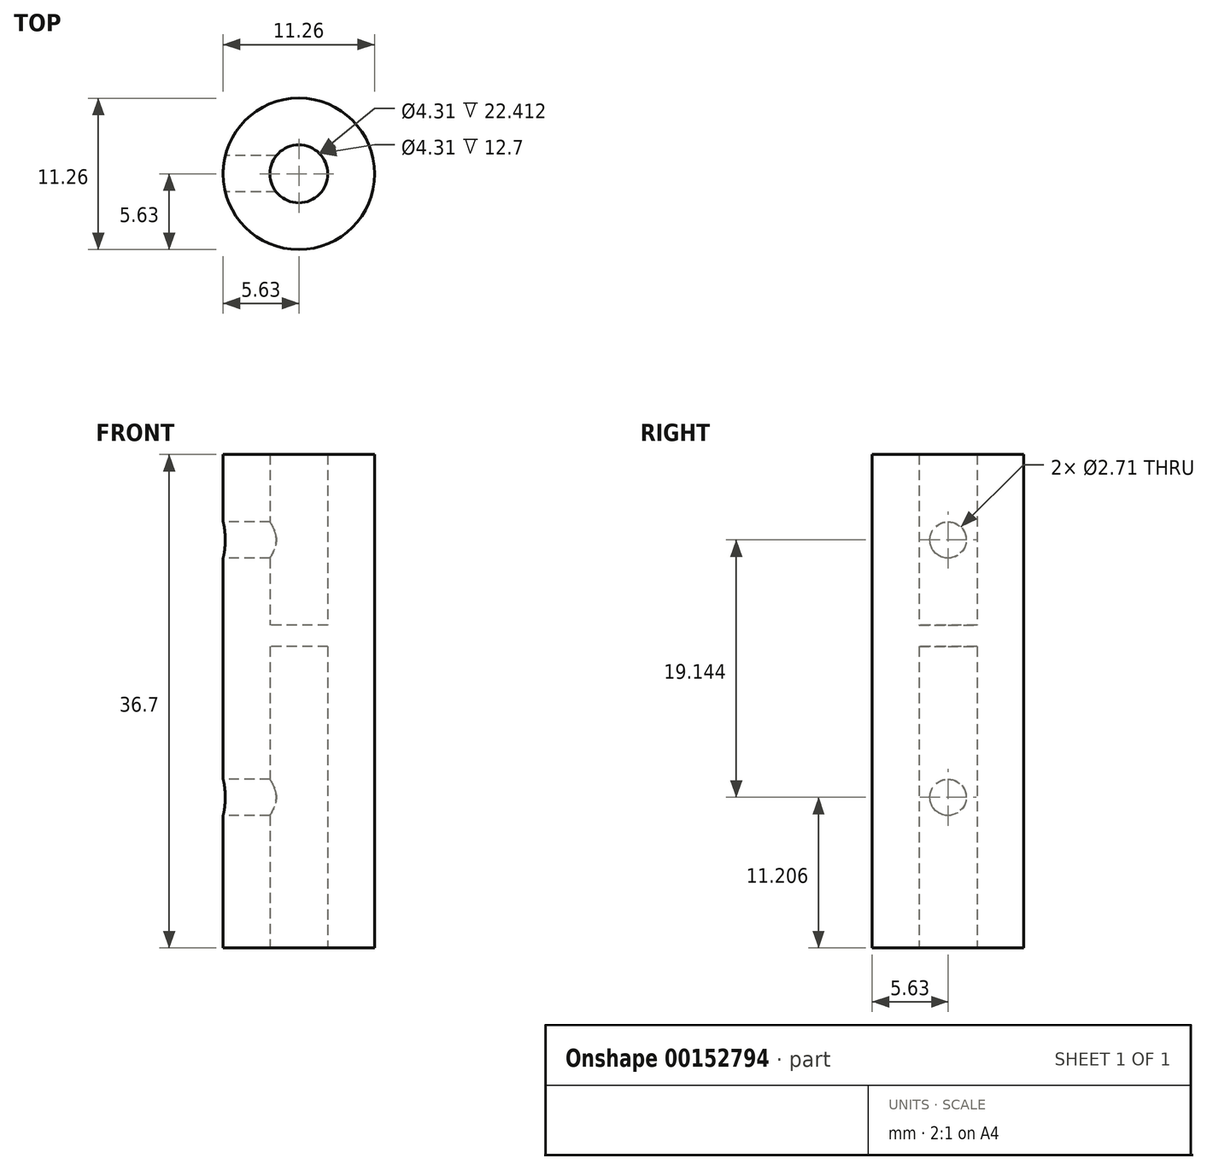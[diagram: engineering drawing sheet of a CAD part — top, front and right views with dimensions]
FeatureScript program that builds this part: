
annotation { "Feature Type Name" : "Feature", "Feature Type Description" : "" }
export const myFeature = defineFeature(function(context is Context, id is Id, definition is map)
    precondition{}
    {
        {
            var Q0;
            Q0=qCreatedBy(makeId("Top.planeOp"),FACE);
            var sketch = newSketch(context, id + "F0", { "sketchPlane" : qUnion([Q0])});
            skLineSegment(sketch, "E0.bottom", {"start": v(5.63, -5.63) * mm, "end": v(-5.63, -5.63) * mm});
            skLineSegment(sketch, "E0.top", {"start": v(5.63, 5.63) * mm, "end": v(-5.63, 5.63) * mm});
            skLineSegment(sketch, "E0.left", {"start": v(5.63, -5.63) * mm, "end": v(5.63, 5.63) * mm});
            skLineSegment(sketch, "E0.right", {"start": v(-5.63, -5.63) * mm, "end": v(-5.63, 5.63) * mm});
            skPoint(sketch, "E0.middle", {"position": v(0, 0) * mm});
            skCircle(sketch, "E1", {"center": v(0, 0) * mm, "radius": 5.63 * mm, "construction": true});
            skCircle(sketch, "E2", {"center": v(0, 0) * mm, "radius": 2.15 * mm});
            skLineSegment(sketch, "E3.bottom", {"start": v(2.15, 1.83) * mm, "end": v(5.33, 1.83) * mm, "construction": true});
            skLineSegment(sketch, "E3.top", {"start": v(2.15, -1.83) * mm, "end": v(5.33, -1.83) * mm, "construction": true});
            skLineSegment(sketch, "E3.left", {"start": v(2.15, 1.83) * mm, "end": v(2.15, -1.83) * mm, "construction": true});
            skLineSegment(sketch, "E3.right", {"start": v(5.33, 1.83) * mm, "end": v(5.33, -1.83) * mm, "construction": true});
            skLineSegment(sketch, "E4", {"start": v(2.15, 0) * mm, "end": v(0, 0) * mm, "construction": true});
            skSolve(sketch);
        }
        {
            var Q0;
            Q0=qSketchRegion(id+"F0",true);
            extrude(context, id + "F1", {"entities" : qUnion([Q0]), "depth" : 22.41 * mm});
        }
        {
            var Q0;
            Q0=makeQuery(id+"F1.opExtrude","CAP_FACE",FACE,{"disambiguationData":[OSD([sQuery(id+"F0.wireOp",EDGE,"E0.bottom"),sQuery(id+"F0.wireOp",EDGE,"E0.top"),sQuery(id+"F0.wireOp",EDGE,"E0.left"),sQuery(id+"F0.wireOp",EDGE,"E0.right"),sQuery(id+"F0.wireOp",EDGE,"E2")])],"isStart":false});
            var sketch = newSketch(context, id + "F2", { "sketchPlane" : qUnion([Q0])});
            skLineSegment(sketch, "E5.bottom", {"start": v(-5.63, 5.63) * mm, "end": v(5.63, 5.63) * mm});
            skLineSegment(sketch, "E5.top", {"start": v(-5.63, -5.63) * mm, "end": v(5.63, -5.63) * mm});
            skLineSegment(sketch, "E5.left", {"start": v(-5.63, 5.63) * mm, "end": v(-5.63, -5.63) * mm});
            skLineSegment(sketch, "E5.right", {"start": v(5.63, 5.63) * mm, "end": v(5.63, -5.63) * mm});
            skPoint(sketch, "E5.middle", {"position": v(0, 0) * mm});
            skSolve(sketch);
        }
        {
            var Q0;
            Q0=qSketchRegion(id+"F2",true);
            extrude(context, id + "F3", {"entities" : qUnion([Q0]), "operationType" : NewBodyOperationType.ADD, "depth" : 1.59 * mm});
        }
        {
            var Q0;
            Q0=makeQuery(id+"F3.opExtrude","CAP_FACE",FACE,{"disambiguationData":[OSD([sQuery(id+"F2.wireOp",EDGE,"E5.bottom"),sQuery(id+"F2.wireOp",EDGE,"E5.top"),sQuery(id+"F2.wireOp",EDGE,"E5.left"),sQuery(id+"F2.wireOp",EDGE,"E5.right")])],"isStart":false});
            var sketch = newSketch(context, id + "F4", { "sketchPlane" : qUnion([Q0])});
            skLineSegment(sketch, "E6.bottom", {"start": v(-5.63, 5.63) * mm, "end": v(5.63, 5.63) * mm});
            skLineSegment(sketch, "E6.top", {"start": v(-5.63, -5.63) * mm, "end": v(5.63, -5.63) * mm});
            skLineSegment(sketch, "E6.left", {"start": v(-5.63, 5.63) * mm, "end": v(-5.63, -5.63) * mm});
            skLineSegment(sketch, "E6.right", {"start": v(5.63, 5.63) * mm, "end": v(5.63, -5.63) * mm});
            skPoint(sketch, "E6.middle", {"position": v(0, 0) * mm});
            skCircle(sketch, "E7", {"center": v(0, 0) * mm, "radius": 2.15 * mm});
            skSolve(sketch);
        }
        {
            var Q0;
            Q0=qSketchRegion(id+"F4",true);
            extrude(context, id + "F5", {"entities" : qUnion([Q0]), "operationType" : NewBodyOperationType.ADD, "depth" : 12.7 * mm});
        }
        {
            var Q0;
            Q0=makeQuery(id+"F5.boolean.opBoolean","MERGE",FACE,{"derivedFrom":[makeQuery(id+"F3.boolean.opBoolean","MERGE",FACE,{"derivedFrom":[makeQuery(id+"F1.opExtrude","SWEPT_FACE",FACE,{"disambiguationData":[OSD([sQuery(id+"F0.wireOp",EDGE,"E0.right")])]}),makeQuery(id+"F3.opExtrude","SWEPT_FACE",FACE,{"disambiguationData":[OSD([sQuery(id+"F2.wireOp",EDGE,"E5.left")])]})]}),makeQuery(id+"F5.opExtrude","SWEPT_FACE",FACE,{"disambiguationData":[OSD([sQuery(id+"F4.wireOp",EDGE,"E6.left")])]})]});
            var sketch = newSketch(context, id + "F6", { "sketchPlane" : qUnion([Q0])});
            skLineSegment(sketch, "E8", {"start": v(0, 36.7) * mm, "end": v(0, 24) * mm, "construction": true});
            skLineSegment(sketch, "E9", {"start": v(0, 0) * mm, "end": v(0, 22.41) * mm, "construction": true});
            skCircle(sketch, "E10", {"center": v(0, 11.2) * mm, "radius": 1.35 * mm});
            skCircle(sketch, "E11", {"center": v(0, 30.35) * mm, "radius": 1.35 * mm});
            skSolve(sketch);
        }
        {
            var Q0;
            Q0=qSketchRegion(id+"F6",true);
            var Q1;
            Q1=makeQuery(id+"F1.opExtrude","SWEPT_FACE",FACE,{"disambiguationData":[OSD([sQuery(id+"F0.wireOp",EDGE,"E2")])]});
            extrude(context, id + "F7", {"entities" : qUnion([Q0]), "operationType" : NewBodyOperationType.REMOVE, "endBound" : BoundingType.UP_TO_SURFACE, "oppositeDirection" : true, "endBoundEntityFace" : qUnion([Q1]), "depth" : 25.4 * mm});
        }
        {
            var Q0;
            Q0=makeQuery(id+"F5.boolean.opBoolean","MERGE",EDGE,{"derivedFrom":[makeQuery(id+"F3.boolean.opBoolean","MERGE",EDGE,{"derivedFrom":[makeQuery(id+"F1.opExtrude","SWEPT_EDGE",EDGE,{"disambiguationData":[OSD([sQuery(id+"F0.wireOp",EDGE,"E0.top"),sQuery(id+"F0.wireOp",EDGE,"E0.right")])]}),makeQuery(id+"F3.opExtrude","SWEPT_EDGE",EDGE,{"disambiguationData":[OSD([sQuery(id+"F2.wireOp",EDGE,"E5.bottom"),sQuery(id+"F2.wireOp",EDGE,"E5.left")])]})]}),makeQuery(id+"F5.opExtrude","SWEPT_EDGE",EDGE,{"disambiguationData":[OSD([sQuery(id+"F4.wireOp",EDGE,"E6.bottom"),sQuery(id+"F4.wireOp",EDGE,"E6.left")])]})]});
            var Q1;
            Q1=makeQuery(id+"F5.boolean.opBoolean","MERGE",EDGE,{"derivedFrom":[makeQuery(id+"F3.boolean.opBoolean","MERGE",EDGE,{"derivedFrom":[makeQuery(id+"F1.opExtrude","SWEPT_EDGE",EDGE,{"disambiguationData":[OSD([sQuery(id+"F0.wireOp",EDGE,"E0.top"),sQuery(id+"F0.wireOp",EDGE,"E0.left")])]}),makeQuery(id+"F3.opExtrude","SWEPT_EDGE",EDGE,{"disambiguationData":[OSD([sQuery(id+"F2.wireOp",EDGE,"E5.bottom"),sQuery(id+"F2.wireOp",EDGE,"E5.right")])]})]}),makeQuery(id+"F5.opExtrude","SWEPT_EDGE",EDGE,{"disambiguationData":[OSD([sQuery(id+"F4.wireOp",EDGE,"E6.bottom"),sQuery(id+"F4.wireOp",EDGE,"E6.right")])]})]});
            var Q2;
            Q2=makeQuery(id+"F5.boolean.opBoolean","MERGE",EDGE,{"derivedFrom":[makeQuery(id+"F3.boolean.opBoolean","MERGE",EDGE,{"derivedFrom":[makeQuery(id+"F1.opExtrude","SWEPT_EDGE",EDGE,{"disambiguationData":[OSD([sQuery(id+"F0.wireOp",EDGE,"E0.bottom"),sQuery(id+"F0.wireOp",EDGE,"E0.right")])]}),makeQuery(id+"F3.opExtrude","SWEPT_EDGE",EDGE,{"disambiguationData":[OSD([sQuery(id+"F2.wireOp",EDGE,"E5.top"),sQuery(id+"F2.wireOp",EDGE,"E5.left")])]})]}),makeQuery(id+"F5.opExtrude","SWEPT_EDGE",EDGE,{"disambiguationData":[OSD([sQuery(id+"F4.wireOp",EDGE,"E6.top"),sQuery(id+"F4.wireOp",EDGE,"E6.left")])]})]});
            var Q3;
            Q3=makeQuery(id+"F5.boolean.opBoolean","MERGE",EDGE,{"derivedFrom":[makeQuery(id+"F3.boolean.opBoolean","MERGE",EDGE,{"derivedFrom":[makeQuery(id+"F1.opExtrude","SWEPT_EDGE",EDGE,{"disambiguationData":[OSD([sQuery(id+"F0.wireOp",EDGE,"E0.bottom"),sQuery(id+"F0.wireOp",EDGE,"E0.left")])]}),makeQuery(id+"F3.opExtrude","SWEPT_EDGE",EDGE,{"disambiguationData":[OSD([sQuery(id+"F2.wireOp",EDGE,"E5.top"),sQuery(id+"F2.wireOp",EDGE,"E5.right")])]})]}),makeQuery(id+"F5.opExtrude","SWEPT_EDGE",EDGE,{"disambiguationData":[OSD([sQuery(id+"F4.wireOp",EDGE,"E6.top"),sQuery(id+"F4.wireOp",EDGE,"E6.right")])]})]});
            fillet(context, id + "F8", {"entities" : qUnion([Q0, Q1, Q2, Q3]), "radius" : 5.63 * mm, "tangentPropagation" : true, "allowEdgeOverflow" : false});
        }
    });
